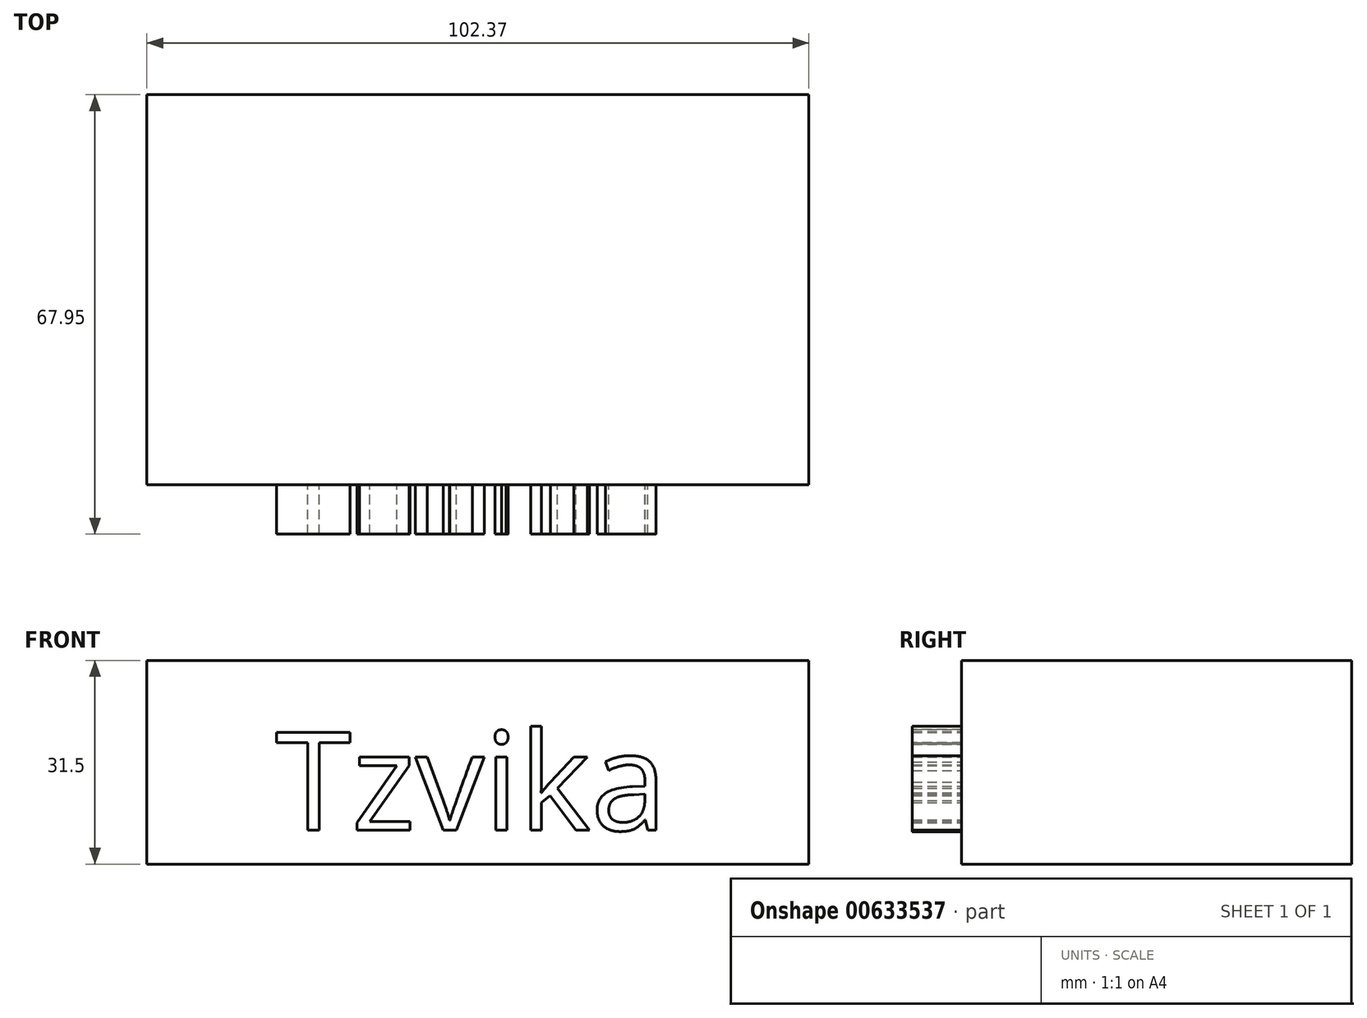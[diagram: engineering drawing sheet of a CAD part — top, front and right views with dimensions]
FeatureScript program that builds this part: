
annotation { "Feature Type Name" : "Feature", "Feature Type Description" : "" }
export const myFeature = defineFeature(function(context is Context, id is Id, definition is map)
    precondition{}
    {
        {
            var Q0;
            Q0=qCreatedBy(makeId("Top.planeOp"),FACE);
            var sketch = newSketch(context, id + "F0", { "sketchPlane" : qUnion([Q0])});
            skLineSegment(sketch, "E0.bottom", {"start": v(-48.16, 30.18) * mm, "end": v(54.21, 30.18) * mm});
            skLineSegment(sketch, "E0.top", {"start": v(-48.16, -30.15) * mm, "end": v(54.21, -30.15) * mm});
            skLineSegment(sketch, "E0.left", {"start": v(-48.16, 30.18) * mm, "end": v(-48.16, -30.15) * mm});
            skLineSegment(sketch, "E0.right", {"start": v(54.21, 30.18) * mm, "end": v(54.21, -30.15) * mm});
            skSolve(sketch);
        }
        {
            var Q0;
            Q0 = qSketchRegion(id + "F0", true);
            var Q1;
            Q1=makeQuery(id+"F0.imprint","IMPRINT",FACE,{"disambiguationData":[TD([[makeQuery(id+"F0.imprint","IMPRINT",EDGE,{"derivedFrom":sQuery(id+"F0.wireOp",EDGE,"E0.bottom")}),-1.0]])]});
            extrude(context, id + "F1", {"entities" : qUnion([Q0, Q1]), "depth" : 31.5 * mm, "offsetDistance" : 25.4 * mm});
        }
        {
            var Q0;
            Q0=qCreatedBy(makeId("Front.planeOp"),FACE);
            var sketch = newSketch(context, id + "F2", { "sketchPlane" : qUnion([Q0])});
            skFitSpline(sketch, "E1", {"points": [v(1.16, 43.2) * mm, v(35.51, 78.62) * mm, v(41.5, 120.11) * mm], "startDerivative": vector(73.08, 67.6) * mm, "endDerivative": vector(0.82, 89.7) * mm});
            skFitSpline(sketch, "E2.0", {"points": [v(3.92, 40.21) * mm, v(6.9, 42.96) * mm, v(13.17, 48.38) * mm, v(21.09, 55.2) * mm, v(27.06, 60.88) * mm, v(31.25, 65.32) * mm, v(34.41, 69.22) * mm, v(36.68, 72.5) * mm, v(38.23, 75.04) * mm, v(39.62, 77.68) * mm, v(40.82, 80.38) * mm, v(41.84, 83.12) * mm, v(42.98, 86.83) * mm, v(44.03, 91.54) * mm, v(44.83, 97.27) * mm, v(45.27, 103.02) * mm, v(45.53, 110.68) * mm, v(45.52, 116.37) * mm, v(45.56, 120.08) * mm]});
            skLineSegment(sketch, "E2.1", {"start": v(4.06, 31.5) * mm, "end": v(4.06, 40.34) * mm});
            skLineSegment(sketch, "E3", {"start": v(41.5, 120.11) * mm, "end": v(45.56, 120.08) * mm});
            skLineSegment(sketch, "E4", {"start": v(0, 31.5) * mm, "end": v(4.06, 31.5) * mm});
            skLineSegment(sketch, "E5", {"start": v(1.16, 43.2) * mm, "end": v(1.16, 31.5) * mm});
            skLineSegment(sketch, "E6", {"start": v(0, 67.85) * mm, "end": v(0, 26.76) * mm, "construction": true});
            skSolve(sketch);
        }
        {
            var Q0;
            Q0=sQuery(id+"F2.wireOp",EDGE,"E1");
            var Q1;
            Q1=sQuery(id+"F2.wireOp",EDGE,"E2.1");
            var Q2;
            Q2=sQuery(id+"F2.wireOp",EDGE,"sKM742RA-1611-XhGz-1y1k-cCwsahDRaDrV");
            var Q3;
            Q3=sQuery(id+"F2.wireOp",EDGE,"E4");
            var Q4;
            Q4=sQuery(id+"F2.wireOp",EDGE,"E2.0");
            var Q5;
            Q5=sQuery(id+"F2.wireOp",EDGE,"E3");
            var Q6;
            Q6=sQuery(id+"F2.wireOp",EDGE,"E6");
            revolve(context, id + "F3", {"bodyType" : ToolBodyType.SURFACE, "surfaceEntities" : qUnion([Q0, Q1, Q2, Q3, Q4, Q5]), "axis" : qUnion([Q6]), "revolveType" : RevolveType.FULL});
        }
        {
            var Q0;
            Q0=makeQuery(id+"F1.opExtrude","SWEPT_FACE",FACE,{"disambiguationData":[OSD([sQuery(id+"F0.wireOp",EDGE,"E0.top")])]});
            var sketch = newSketch(context, id + "F4", { "sketchPlane" : qUnion([Q0])});
            skText(sketch, "E7", { "text": "Tzvika", "fontName": "OpenSans-Regular.ttf"});
            const initialGuessF4  = {"E7": [-0.02826, 0.00523, 1, 0, 0.01526]};
            skSetInitialGuess(sketch, initialGuessF4);
            skSolve(sketch);
        }
        {
            var Q0;
            Q0 = qSketchRegion(id + "F4", true);
            extrude(context, id + "F5", {"entities" : qUnion([Q0]), "operationType" : NewBodyOperationType.ADD, "depth" : 7.62 * mm, "offsetDistance" : 25.4 * mm});
        }
    });
